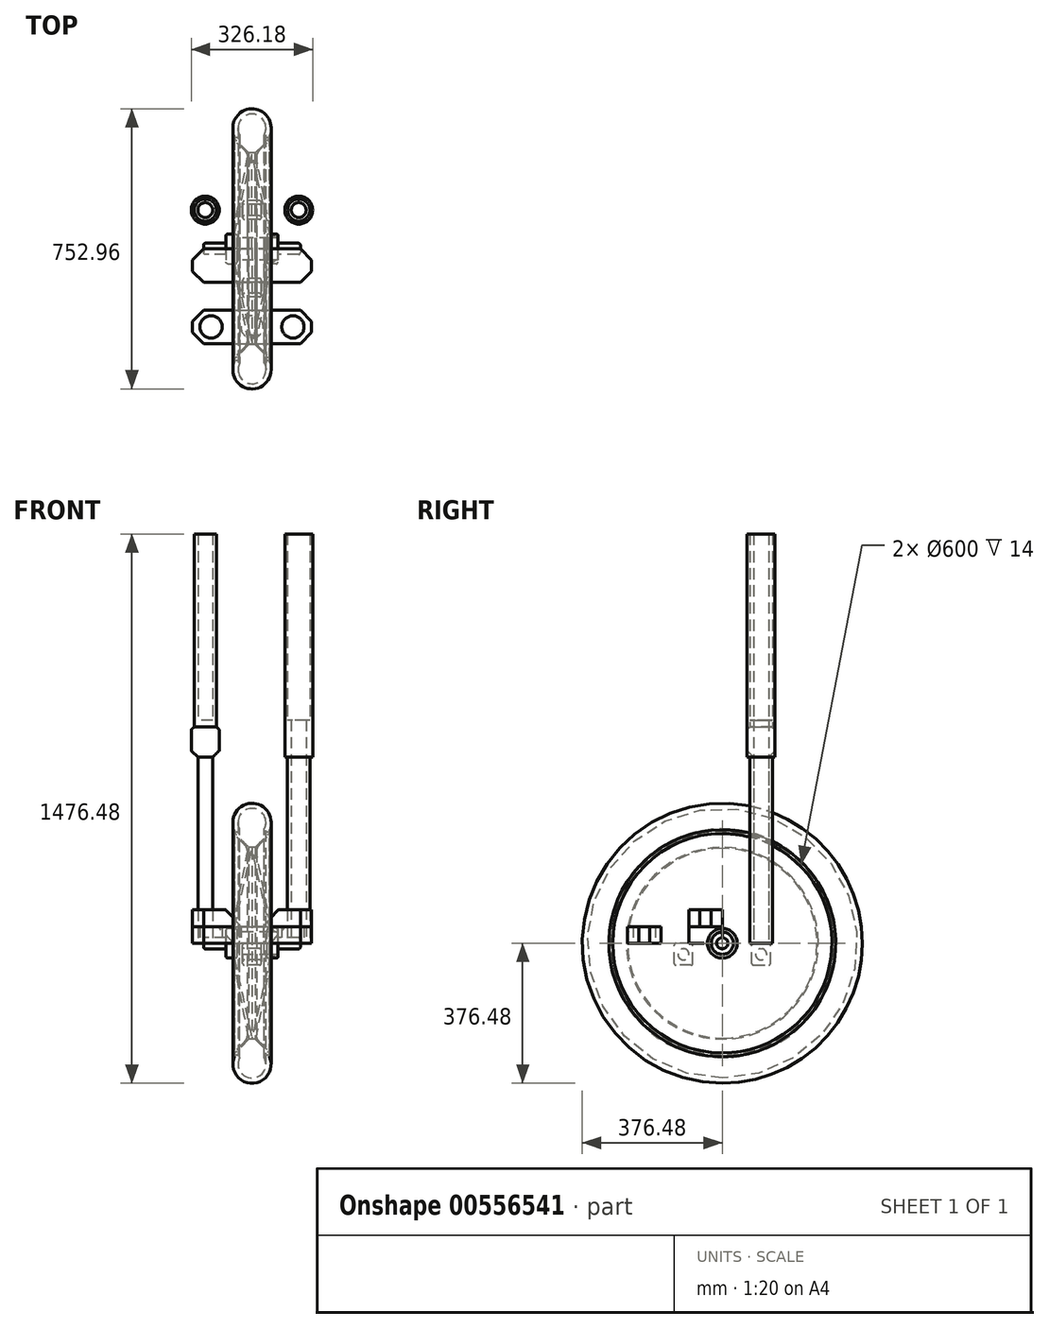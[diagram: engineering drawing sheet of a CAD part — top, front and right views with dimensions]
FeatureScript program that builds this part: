
annotation { "Feature Type Name" : "Feature", "Feature Type Description" : "" }
export const myFeature = defineFeature(function(context is Context, id is Id, definition is map)
    precondition{}
    {
        {
            var Q0;
            Q0=qCreatedBy(makeId("Front.planeOp"),FACE);
            var sketch = newSketch(context, id + "F0", { "sketchPlane" : qUnion([Q0])});
            skLineSegment(sketch, "E0", {"start": v(0, 0) * mm, "end": v(0, 304.8) * mm, "construction": true});
            skLineSegment(sketch, "E1", {"start": v(0, 0) * mm, "end": v(0, 254.8) * mm, "construction": true});
            skLineSegment(sketch, "E2", {"start": v(0, 304.8) * mm, "end": v(-50, 304.8) * mm, "construction": true});
            skLineSegment(sketch, "E3", {"start": v(0, 304.8) * mm, "end": v(50, 304.8) * mm, "construction": true});
            skPoint(sketch, "E4", {"position": v(-50, 304.8) * mm});
            skPoint(sketch, "E5", {"position": v(50, 304.8) * mm});
            skLineSegment(sketch, "E6", {"start": v(-50, 294.8) * mm, "end": v(-10, 254.8) * mm});
            skLineSegment(sketch, "E7", {"start": v(-50, 294.8) * mm, "end": v(-50, 304.8) * mm});
            skLineSegment(sketch, "E8", {"start": v(-10, 254.8) * mm, "end": v(0, 254.8) * mm});
            skLineSegment(sketch, "E9", {"start": v(50, 304.8) * mm, "end": v(50, 294.8) * mm});
            skLineSegment(sketch, "E10", {"start": v(50, 294.8) * mm, "end": v(10, 254.8) * mm});
            skLineSegment(sketch, "E11", {"start": v(10, 254.8) * mm, "end": v(0, 254.8) * mm});
            skLineSegment(sketch, "E12.0", {"start": v(-47, 296.04) * mm, "end": v(-47, 304.8) * mm});
            skLineSegment(sketch, "E12.1", {"start": v(-47, 296.04) * mm, "end": v(-8.76, 257.8) * mm});
            skLineSegment(sketch, "E12.2", {"start": v(47, 304.8) * mm, "end": v(47, 296.04) * mm});
            skLineSegment(sketch, "E12.3", {"start": v(47, 296.04) * mm, "end": v(8.76, 257.8) * mm});
            skLineSegment(sketch, "E12.4", {"start": v(8.76, 257.8) * mm, "end": v(0, 257.8) * mm});
            skLineSegment(sketch, "E12.5", {"start": v(-8.76, 257.8) * mm, "end": v(0, 257.8) * mm});
            skLineSegment(sketch, "E13", {"start": v(-47, 304.8) * mm, "end": v(-50, 304.8) * mm});
            skLineSegment(sketch, "E14", {"start": v(47, 304.8) * mm, "end": v(50, 304.8) * mm});
            skLineSegment(sketch, "E15", {"start": v(0, 0) * mm, "end": v(125, 0) * mm, "construction": true});
            skLineSegment(sketch, "E16", {"start": v(-10, 254.8) * mm, "end": v(-55.27, 19.77) * mm});
            skLineSegment(sketch, "E17", {"start": v(-55.27, 19.77) * mm, "end": v(-52.26, 19.55) * mm});
            skLineSegment(sketch, "E18", {"start": v(-52.26, 19.55) * mm, "end": v(0, 254.8) * mm});
            skLineSegment(sketch, "E19.MirrorCS", {"start": v(52.26, 19.55) * mm, "end": v(0, 254.8) * mm});
            skLineSegment(sketch, "E20.MirrorCS", {"start": v(10, 254.8) * mm, "end": v(55.27, 19.77) * mm});
            skLineSegment(sketch, "E21.MirrorCS", {"start": v(55.27, 19.77) * mm, "end": v(52.26, 19.55) * mm});
            skSolve(sketch);
        }
        {
            var Q0;
            Q0=qSketchRegion(id+"F0",true);
            var Q1;
            Q1=sQuery(id+"F0.wireOp",EDGE,"E15");
            revolve(context, id + "F1", {"entities" : qUnion([Q0]), "axis" : qUnion([Q1]), "revolveType" : RevolveType.FULL});
        }
        {
            var Q0;
            Q0=qCreatedBy(makeId("Right.planeOp"),FACE);
            var sketch = newSketch(context, id + "F2", { "sketchPlane" : qUnion([Q0])});
            skCircle(sketch, "E22", {"center": v(0, 0) * mm, "radius": 15 * mm});
            skSolve(sketch);
        }
        {
            var Q0;
            Q0=qSketchRegion(id+"F2",true);
            extrude(context, id + "F3", {"entities" : qUnion([Q0]), "endBound" : BoundingType.SYMMETRIC, "depth" : 260 * mm, "offsetDistance" : 25 * mm});
        }
        {
            var Q0;
            Q0=qCreatedBy(makeId("Right.planeOp"),FACE);
            var sketch = newSketch(context, id + "F4", { "sketchPlane" : qUnion([Q0])});
            skCircle(sketch, "E23", {"center": v(0, 0) * mm, "radius": 15 * mm});
            skCircle(sketch, "E24", {"center": v(0, 0) * mm, "radius": 20 * mm});
            skCircle(sketch, "E25", {"center": v(0, 0) * mm, "radius": 30 * mm});
            skCircle(sketch, "E26", {"center": v(0, 0) * mm, "radius": 40 * mm});
            skPoint(sketch, "E27", {"position": v(0, 32.5) * mm});
            skLineSegment(sketch, "E28", {"start": v(0, 0) * mm, "end": v(11.12, 30.54) * mm, "construction": true});
            skPoint(sketch, "E29", {"position": v(11.12, 30.54) * mm});
            skLineSegment(sketch, "E30", {"start": v(0, 0) * mm, "end": v(20.9, 24.9) * mm, "construction": true});
            skLineSegment(sketch, "E31", {"start": v(0, 0) * mm, "end": v(28.15, 16.25) * mm, "construction": true});
            skLineSegment(sketch, "E32", {"start": v(0, 0) * mm, "end": v(32, 5.64) * mm, "construction": true});
            skLineSegment(sketch, "E33", {"start": v(0, 0) * mm, "end": v(32, -5.64) * mm, "construction": true});
            skLineSegment(sketch, "E34", {"start": v(0, 0) * mm, "end": v(28.15, -16.25) * mm, "construction": true});
            skLineSegment(sketch, "E35", {"start": v(0, 0) * mm, "end": v(20.9, -24.9) * mm, "construction": true});
            skLineSegment(sketch, "E36", {"start": v(0, 0) * mm, "end": v(0, -32.5) * mm, "construction": true});
            skLineSegment(sketch, "E37", {"start": v(0, 0) * mm, "end": v(-11.12, -30.54) * mm, "construction": true});
            skLineSegment(sketch, "E38", {"start": v(0, 0) * mm, "end": v(-20.9, -24.9) * mm, "construction": true});
            skLineSegment(sketch, "E39", {"start": v(0, 0) * mm, "end": v(-32, -5.64) * mm, "construction": true});
            skLineSegment(sketch, "E40", {"start": v(0, 0) * mm, "end": v(-32, 5.64) * mm, "construction": true});
            skLineSegment(sketch, "E41", {"start": v(0, 0) * mm, "end": v(-20.9, 24.9) * mm, "construction": true});
            skLineSegment(sketch, "E42", {"start": v(0, 0) * mm, "end": v(-28.15, -16.25) * mm, "construction": true});
            skLineSegment(sketch, "E43", {"start": v(0, 0) * mm, "end": v(11.12, -30.54) * mm, "construction": true});
            skLineSegment(sketch, "E44", {"start": v(0, 0) * mm, "end": v(-28.15, 16.25) * mm, "construction": true});
            skLineSegment(sketch, "E45", {"start": v(0, 0) * mm, "end": v(-11.12, 30.54) * mm, "construction": true});
            skPoint(sketch, "E46", {"position": v(20.9, 24.9) * mm});
            skPoint(sketch, "E47", {"position": v(28.15, 16.25) * mm});
            skPoint(sketch, "E48", {"position": v(32, 5.64) * mm});
            skPoint(sketch, "E49", {"position": v(32, -5.64) * mm});
            skPoint(sketch, "E50", {"position": v(28.15, -16.25) * mm});
            skPoint(sketch, "E51", {"position": v(20.9, -24.9) * mm});
            skPoint(sketch, "E52", {"position": v(11.12, -30.54) * mm});
            skPoint(sketch, "E53", {"position": v(0, -32.5) * mm});
            skPoint(sketch, "E54", {"position": v(-11.12, -30.54) * mm});
            skPoint(sketch, "E55", {"position": v(-20.9, -24.9) * mm});
            skPoint(sketch, "E56", {"position": v(-28.15, -16.25) * mm});
            skPoint(sketch, "E57", {"position": v(-32, -5.64) * mm});
            skPoint(sketch, "E58", {"position": v(-32, 5.64) * mm});
            skPoint(sketch, "E59", {"position": v(-28.15, 16.25) * mm});
            skPoint(sketch, "E60", {"position": v(-20.9, 24.9) * mm});
            skPoint(sketch, "E61", {"position": v(-11.12, 30.54) * mm});
            skSolve(sketch);
        }
        {
            var Q0;
            Q0=makeQuery(id+"F4.imprint","IMPRINT",FACE,{"disambiguationData":[TD([[makeQuery(id+"F4.imprint","IMPRINT",EDGE,{"derivedFrom":sQuery(id+"F4.wireOp",EDGE,"E23")}),-1.0]])]});
            extrude(context, id + "F5", {"entities" : qUnion([Q0]), "operationType" : NewBodyOperationType.ADD, "endBound" : BoundingType.SYMMETRIC, "depth" : 140 * mm, "offsetDistance" : 25 * mm});
        }
        {
            var Q0;
            Q0=makeQuery(id+"F4.imprint","IMPRINT",FACE,{"disambiguationData":[TD([[makeQuery(id+"F4.imprint","IMPRINT",EDGE,{"derivedFrom":sQuery(id+"F4.wireOp",EDGE,"E24")}),-1.0]])]});
            extrude(context, id + "F6", {"entities" : qUnion([Q0]), "operationType" : NewBodyOperationType.ADD, "endBound" : BoundingType.SYMMETRIC, "depth" : 140 * mm, "offsetDistance" : 25 * mm});
        }
        {
            var Q0;
            Q0=makeQuery(id+"F4.imprint","IMPRINT",FACE,{"disambiguationData":[TD([[makeQuery(id+"F4.imprint","IMPRINT",EDGE,{"derivedFrom":sQuery(id+"F4.wireOp",EDGE,"E25")}),-1.0]])]});
            var Q1;
            Q1=makeQuery(id+"F5.opExtrude","CAP_FACE",FACE,{"disambiguationData":[OSD([sQuery(id+"F4.wireOp",EDGE,"E23"),sQuery(id+"F4.wireOp",EDGE,"E24")])],"isStart":false});
            extrude(context, id + "F7", {"entities" : qUnion([Q0]), "endBound" : BoundingType.UP_TO_SURFACE, "depth" : 182 * mm, "endBoundEntityFace" : qUnion([Q1]), "offsetDistance" : 25 * mm, "hasSecondDirection" : true, "secondDirectionOppositeDirection" : false, "secondDirectionDepth" : 40 * mm});
        }
        {
            var Q0;
            Q0=makeQuery(id+"F4.imprint","IMPRINT",FACE,{"disambiguationData":[TD([[makeQuery(id+"F4.imprint","IMPRINT",EDGE,{"derivedFrom":sQuery(id+"F4.wireOp",EDGE,"E25")}),-1.0]])]});
            var Q1;
            Q1=makeQuery(id+"F5.opExtrude","CAP_FACE",FACE,{"disambiguationData":[OSD([sQuery(id+"F4.wireOp",EDGE,"E23"),sQuery(id+"F4.wireOp",EDGE,"E24")])],"isStart":true});
            extrude(context, id + "F8", {"entities" : qUnion([Q0]), "operationType" : NewBodyOperationType.ADD, "endBound" : BoundingType.UP_TO_SURFACE, "oppositeDirection" : true, "depth" : 25 * mm, "endBoundEntityFace" : qUnion([Q1]), "offsetDistance" : 25 * mm, "hasSecondDirection" : true, "secondDirectionOppositeDirection" : true, "secondDirectionDepth" : 40 * mm});
        }
        {
            var Q0;
            Q0=makeQuery(id+"F3.opExtrude","CAP_EDGE",EDGE,{"disambiguationData":[OSD([sQuery(id+"F2.wireOp",EDGE,"E22")])],"isStart":false});
            var Q1;
            Q1=makeQuery(id+"F3.opExtrude","CAP_EDGE",EDGE,{"disambiguationData":[OSD([sQuery(id+"F2.wireOp",EDGE,"E22")])],"isStart":true});
            var Q2;
            Q2=makeQuery(id+"F6.opExtrude","CAP_EDGE",EDGE,{"disambiguationData":[OSD([sQuery(id+"F4.wireOp",EDGE,"E25")])],"isStart":true});
            var Q3;
            Q3=makeQuery(id+"F6.opExtrude","CAP_EDGE",EDGE,{"disambiguationData":[OSD([sQuery(id+"F4.wireOp",EDGE,"E25")])],"isStart":false});
            var Q4;
            Q4=makeQuery(id+"F8.opExtrude","CAP_EDGE",EDGE,{"disambiguationData":[OSD([sQuery(id+"F4.wireOp",EDGE,"E26")])],"isStart":false});
            var Q5;
            Q5=makeQuery(id+"F8.opExtrude","CAP_EDGE",EDGE,{"disambiguationData":[OSD([sQuery(id+"F4.wireOp",EDGE,"E26")])],"isStart":true});
            var Q6;
            Q6=makeQuery(id+"F7.opExtrude","CAP_EDGE",EDGE,{"disambiguationData":[OSD([sQuery(id+"F4.wireOp",EDGE,"E26")])],"isStart":true});
            var Q7;
            Q7=makeQuery(id+"F7.opExtrude","CAP_EDGE",EDGE,{"disambiguationData":[OSD([sQuery(id+"F4.wireOp",EDGE,"E26")])],"isStart":false});
            fillet(context, id + "F9", {"entities" : qUnion([Q0, Q1, Q2, Q3, Q4, Q5, Q6, Q7]), "radius" : 5 * mm, "tangentPropagation" : true, "allowEdgeOverflow" : false});
        }
        {
            var Q0;
            Q0=qCreatedBy(makeId("Top.planeOp"),FACE);
            var sketch = newSketch(context, id + "F10", { "sketchPlane" : qUnion([Q0])});
            skCircle(sketch, "E62", {"center": v(-125.6, 104.3) * mm, "radius": 20 * mm});
            skCircle(sketch, "E63", {"center": v(-125.6, 104.3) * mm, "radius": 30 * mm});
            skCircle(sketch, "E64", {"center": v(-125.6, 104.3) * mm, "radius": 37.5 * mm});
            skCircle(sketch, "E65.MirrorC", {"center": v(125.6, 104.3) * mm, "radius": 30 * mm});
            skCircle(sketch, "E66.MirrorC", {"center": v(125.6, 104.3) * mm, "radius": 20 * mm});
            skCircle(sketch, "E67.MirrorC", {"center": v(125.6, 104.3) * mm, "radius": 37.5 * mm});
            skSolve(sketch);
        }
        {
            var Q0;
            Q0=makeQuery(id+"F10.imprint","IMPRINT",FACE,{"disambiguationData":[TD([[makeQuery(id+"F10.imprint","IMPRINT",EDGE,{"derivedFrom":sQuery(id+"F10.wireOp",EDGE,"E62")}),1.0]])]});
            var Q1;
            Q1=makeQuery(id+"F10.imprint","IMPRINT",FACE,{"disambiguationData":[TD([[makeQuery(id+"F10.imprint","IMPRINT",EDGE,{"derivedFrom":sQuery(id+"F10.wireOp",EDGE,"E66.MirrorC")}),-1.0]])]});
            extrude(context, id + "F11", {"entities" : qUnion([Q0, Q1]), "depth" : 600 * mm, "offsetDistance" : 25 * mm});
        }
        {
            var Q0;
            Q0=makeQuery(id+"F10.imprint","IMPRINT",FACE,{"disambiguationData":[TD([[makeQuery(id+"F10.imprint","IMPRINT",EDGE,{"derivedFrom":sQuery(id+"F10.wireOp",EDGE,"E62")}),-1.0]])]});
            var Q1;
            Q1=makeQuery(id+"F10.imprint","IMPRINT",FACE,{"disambiguationData":[TD([[makeQuery(id+"F10.imprint","IMPRINT",EDGE,{"derivedFrom":sQuery(id+"F10.wireOp",EDGE,"E65.MirrorC")}),-1.0]])]});
            extrude(context, id + "F12", {"entities" : qUnion([Q0, Q1]), "operationType" : NewBodyOperationType.ADD, "depth" : 1100 * mm, "offsetDistance" : 25 * mm, "hasSecondDirection" : true, "secondDirectionOppositeDirection" : false, "secondDirectionDepth" : 500 * mm});
        }
        {
            var Q0;
            Q0=qCreatedBy(makeId("Right.planeOp"),FACE);
            var sketch = newSketch(context, id + "F13", { "sketchPlane" : qUnion([Q0])});
            skLineSegment(sketch, "E68.bottom", {"start": v(79.37, -59.12) * mm, "end": v(129.37, -59.12) * mm});
            skLineSegment(sketch, "E68.top", {"start": v(79.37, -0.19) * mm, "end": v(129.37, -0.19) * mm});
            skLineSegment(sketch, "E68.left", {"start": v(79.37, -59.12) * mm, "end": v(79.37, -0.19) * mm});
            skLineSegment(sketch, "E68.right", {"start": v(129.37, -59.12) * mm, "end": v(129.37, -0.19) * mm});
            skPoint(sketch, "E68.middle", {"position": v(104.37, -29.65) * mm});
            skCircle(sketch, "E69", {"center": v(104.37, -29.65) * mm, "radius": 15 * mm});
            skPoint(sketch, "E70.MirrorP", {"position": v(-104.37, -29.65) * mm});
            skLineSegment(sketch, "E71.MirrorCS", {"start": v(-129.37, -59.12) * mm, "end": v(-129.37, -0.19) * mm});
            skCircle(sketch, "E72.MirrorC", {"center": v(-104.37, -29.65) * mm, "radius": 15 * mm});
            skLineSegment(sketch, "E73.MirrorCS", {"start": v(-79.37, -59.12) * mm, "end": v(-129.37, -59.12) * mm});
            skLineSegment(sketch, "E74.MirrorCS", {"start": v(-79.37, -59.12) * mm, "end": v(-79.37, -0.19) * mm});
            skLineSegment(sketch, "E75.MirrorCS", {"start": v(-79.37, -0.19) * mm, "end": v(-129.37, -0.19) * mm});
            skSolve(sketch);
        }
        {
            var Q0;
            Q0 = qSketchRegion(id + "F13", true);
            extrude(context, id + "F14", {"entities" : qUnion([Q0]), "endBound" : BoundingType.SYMMETRIC, "depth" : 50 * mm, "offsetDistance" : 25 * mm});
        }
        {
            var Q0;
            Q0=makeQuery(id+"F14.opExtrude","CAP_EDGE",EDGE,{"disambiguationData":[OSD([sQuery(id+"F13.wireOp",EDGE,"E68.top")])],"isStart":false});
            var Q1;
            Q1=makeQuery(id+"F14.opExtrude","SWEPT_EDGE",EDGE,{"disambiguationData":[OSD([sQuery(id+"F13.wireOp",EDGE,"E68.top"),sQuery(id+"F13.wireOp",EDGE,"E68.left")])]});
            var Q2;
            Q2=makeQuery(id+"F14.opExtrude","CAP_EDGE",EDGE,{"disambiguationData":[OSD([sQuery(id+"F13.wireOp",EDGE,"E68.top")])],"isStart":true});
            var Q3;
            Q3=makeQuery(id+"F14.opExtrude","SWEPT_EDGE",EDGE,{"disambiguationData":[OSD([sQuery(id+"F13.wireOp",EDGE,"E68.top"),sQuery(id+"F13.wireOp",EDGE,"E68.right")])]});
            var Q4;
            Q4=makeQuery(id+"F14.opExtrude","SWEPT_FACE",FACE,{"disambiguationData":[OSD([sQuery(id+"F13.wireOp",EDGE,"E68.left")])]});
            var Q5;
            Q5=makeQuery(id+"F14.opExtrude","CAP_FACE",FACE,{"disambiguationData":[OSD([sQuery(id+"F13.wireOp",EDGE,"E68.bottom"),sQuery(id+"F13.wireOp",EDGE,"E68.top"),sQuery(id+"F13.wireOp",EDGE,"E68.left"),sQuery(id+"F13.wireOp",EDGE,"E68.right"),sQuery(id+"F13.wireOp",EDGE,"E69")])],"isStart":false});
            var Q6;
            Q6=makeQuery(id+"F14.opExtrude","SWEPT_FACE",FACE,{"disambiguationData":[OSD([sQuery(id+"F13.wireOp",EDGE,"E68.right")])]});
            var Q7;
            Q7=makeQuery(id+"F14.opExtrude","CAP_FACE",FACE,{"disambiguationData":[OSD([sQuery(id+"F13.wireOp",EDGE,"E68.bottom"),sQuery(id+"F13.wireOp",EDGE,"E68.top"),sQuery(id+"F13.wireOp",EDGE,"E68.left"),sQuery(id+"F13.wireOp",EDGE,"E68.right"),sQuery(id+"F13.wireOp",EDGE,"E69")])],"isStart":true});
            var Q8;
            Q8=makeQuery(id+"F14.opExtrude","CAP_EDGE",EDGE,{"disambiguationData":[OSD([sQuery(id+"F13.wireOp",EDGE,"E72.MirrorC")])],"isStart":false});
            var Q9;
            Q9=makeQuery(id+"F14.opExtrude","CAP_EDGE",EDGE,{"disambiguationData":[OSD([sQuery(id+"F13.wireOp",EDGE,"E71.MirrorCS")])],"isStart":false});
            var Q10;
            Q10=makeQuery(id+"F14.opExtrude","CAP_EDGE",EDGE,{"disambiguationData":[OSD([sQuery(id+"F13.wireOp",EDGE,"E74.MirrorCS")])],"isStart":false});
            var Q11;
            Q11=makeQuery(id+"F14.opExtrude","CAP_EDGE",EDGE,{"disambiguationData":[OSD([sQuery(id+"F13.wireOp",EDGE,"E72.MirrorC")])],"isStart":true});
            var Q12;
            Q12=makeQuery(id+"F14.opExtrude","CAP_EDGE",EDGE,{"disambiguationData":[OSD([sQuery(id+"F13.wireOp",EDGE,"E75.MirrorCS")])],"isStart":false});
            var Q13;
            Q13=makeQuery(id+"F14.opExtrude","CAP_EDGE",EDGE,{"disambiguationData":[OSD([sQuery(id+"F13.wireOp",EDGE,"E73.MirrorCS")])],"isStart":false});
            var Q14;
            Q14=makeQuery(id+"F14.opExtrude","CAP_EDGE",EDGE,{"disambiguationData":[OSD([sQuery(id+"F13.wireOp",EDGE,"E74.MirrorCS")])],"isStart":true});
            var Q15;
            Q15=makeQuery(id+"F14.opExtrude","SWEPT_EDGE",EDGE,{"disambiguationData":[OSD([sQuery(id+"F13.wireOp",EDGE,"E73.MirrorCS"),sQuery(id+"F13.wireOp",EDGE,"E74.MirrorCS")])]});
            var Q16;
            Q16=makeQuery(id+"F14.opExtrude","SWEPT_EDGE",EDGE,{"disambiguationData":[OSD([sQuery(id+"F13.wireOp",EDGE,"E71.MirrorCS"),sQuery(id+"F13.wireOp",EDGE,"E73.MirrorCS")])]});
            var Q17;
            Q17=makeQuery(id+"F14.opExtrude","SWEPT_EDGE",EDGE,{"disambiguationData":[OSD([sQuery(id+"F13.wireOp",EDGE,"E71.MirrorCS"),sQuery(id+"F13.wireOp",EDGE,"E75.MirrorCS")])]});
            var Q18;
            Q18=makeQuery(id+"F14.opExtrude","CAP_EDGE",EDGE,{"disambiguationData":[OSD([sQuery(id+"F13.wireOp",EDGE,"E71.MirrorCS")])],"isStart":true});
            var Q19;
            Q19=makeQuery(id+"F14.opExtrude","SWEPT_EDGE",EDGE,{"disambiguationData":[OSD([sQuery(id+"F13.wireOp",EDGE,"E74.MirrorCS"),sQuery(id+"F13.wireOp",EDGE,"E75.MirrorCS")])]});
            var Q20;
            Q20=makeQuery(id+"F14.opExtrude","CAP_EDGE",EDGE,{"disambiguationData":[OSD([sQuery(id+"F13.wireOp",EDGE,"E75.MirrorCS")])],"isStart":true});
            var Q21;
            Q21=makeQuery(id+"F14.opExtrude","CAP_EDGE",EDGE,{"disambiguationData":[OSD([sQuery(id+"F13.wireOp",EDGE,"E73.MirrorCS")])],"isStart":true});
            fillet(context, id + "F15", {"entities" : qUnion([Q0, Q1, Q2, Q3, Q4, Q5, Q6, Q7, Q8, Q9, Q10, Q11, Q12, Q13, Q14, Q15, Q16, Q17, Q18, Q19, Q20, Q21]), "radius" : 5 * mm, "tangentPropagation" : true, "allowEdgeOverflow" : false});
        }
        {
            var Q0;
            Q0=makeQuery(id+"F1.opRevolve","SWEPT_FACE",FACE,{"disambiguationData":[OSD([sQuery(id+"F0.wireOp",EDGE,"E20.MirrorCS")])]});
            var Q1;
            Q1=makeQuery(id+"F1.opRevolve","SWEPT_EDGE",EDGE,{"disambiguationData":[OSD([sQuery(id+"F0.wireOp",EDGE,"E6"),sQuery(id+"F0.wireOp",EDGE,"E8"),sQuery(id+"F0.wireOp",EDGE,"E16")])]});
            fillet(context, id + "F16", {"entities" : qUnion([Q0, Q1]), "radius" : 25 * mm, "tangentPropagation" : true, "allowEdgeOverflow" : false});
        }
        {
            var Q0;
            Q0=makeQuery(id+"F12.opExtrude","CAP_EDGE",EDGE,{"disambiguationData":[OSD([sQuery(id+"F10.wireOp",EDGE,"E63")])],"isStart":true});
            var Q1;
            Q1=makeQuery(id+"F12.opExtrude","CAP_EDGE",EDGE,{"disambiguationData":[OSD([sQuery(id+"F10.wireOp",EDGE,"E65.MirrorC")])],"isStart":true});
            chamfer(context, id + "F17", {"entities" : qUnion([Q0, Q1]), "width" : 10 * mm, "tangentPropagation" : true});
        }
        {
            var Q0;
            Q0=makeQuery(id+"F10.imprint","IMPRINT",FACE,{"disambiguationData":[TD([[makeQuery(id+"F10.imprint","IMPRINT",EDGE,{"derivedFrom":sQuery(id+"F10.wireOp",EDGE,"E63")}),-1.0]])]});
            var Q1;
            Q1=makeQuery(id+"F10.imprint","IMPRINT",FACE,{"disambiguationData":[TD([[makeQuery(id+"F10.imprint","IMPRINT",EDGE,{"derivedFrom":sQuery(id+"F10.wireOp",EDGE,"E65.MirrorC")}),1.0]])]});
            extrude(context, id + "F18", {"entities" : qUnion([Q0, Q1]), "operationType" : NewBodyOperationType.ADD, "depth" : 581 * mm, "offsetDistance" : 25 * mm, "hasSecondDirection" : true, "secondDirectionOppositeDirection" : false, "secondDirectionDepth" : 509 * mm});
        }
        {
            var Q0;
            Q0=makeQuery(id+"F18.opExtrude","CAP_EDGE",EDGE,{"disambiguationData":[OSD([sQuery(id+"F10.wireOp",EDGE,"E64")])],"isStart":true});
            var Q1;
            Q1=makeQuery(id+"F18.opExtrude","CAP_EDGE",EDGE,{"disambiguationData":[OSD([sQuery(id+"F10.wireOp",EDGE,"E67.MirrorC")])],"isStart":true});
            chamfer(context, id + "F19", {"entities" : qUnion([Q0, Q1]), "width" : 8.5 * mm, "tangentPropagation" : true});
        }
        {
            var Q0;
            Q0=makeQuery(id+"F18.opExtrude","CAP_EDGE",EDGE,{"disambiguationData":[OSD([sQuery(id+"F10.wireOp",EDGE,"E64")])],"isStart":false});
            var Q1;
            Q1=makeQuery(id+"F18.opExtrude","CAP_EDGE",EDGE,{"disambiguationData":[OSD([sQuery(id+"F10.wireOp",EDGE,"E67.MirrorC")])],"isStart":false});
            chamfer(context, id + "F20", {"entities" : qUnion([Q0, Q1]), "width" : 7 * mm, "tangentPropagation" : true});
        }
        {
            var Q0;
            {var subQ0=sQuery(id+"F10.wireOp",EDGE,"E64");Q0=makeQuery(id+"F20.opChamfer","BLEND_EDGE",EDGE,{"blendedFrom":[makeQuery(id+"F18.opExtrude","CAP_EDGE",EDGE,{"disambiguationData":[OSD([subQ0])],"isStart":false}),makeQuery(id+"F18.opExtrude","CAP_FACE",FACE,{"disambiguationData":[OSD([sQuery(id+"F10.wireOp",EDGE,"E63"),subQ0])],"isStart":false})],"blendedInto":[makeQuery(id+"F18.opExtrude","CAP_FACE",FACE,{"disambiguationData":[OSD([sQuery(id+"F10.wireOp",EDGE,"E63"),subQ0])],"isStart":false})]});}
            var Q1;
            {var subQ0=sQuery(id+"F10.wireOp",EDGE,"E64");Q1=makeQuery(id+"F20.opChamfer","BLEND_EDGE",EDGE,{"blendedFrom":[makeQuery(id+"F18.opExtrude","CAP_EDGE",EDGE,{"disambiguationData":[OSD([subQ0])],"isStart":false}),makeQuery(id+"F18.opExtrude","SWEPT_FACE",FACE,{"disambiguationData":[OSD([subQ0])]})],"blendedInto":[makeQuery(id+"F18.opExtrude","SWEPT_FACE",FACE,{"disambiguationData":[OSD([subQ0])]})]});}
            var Q2;
            {var subQ0=sQuery(id+"F10.wireOp",EDGE,"E64");Q2=makeQuery(id+"F19.opChamfer","BLEND_EDGE",EDGE,{"blendedFrom":[makeQuery(id+"F18.opExtrude","CAP_EDGE",EDGE,{"disambiguationData":[OSD([subQ0])],"isStart":true}),makeQuery(id+"F18.opExtrude","SWEPT_FACE",FACE,{"disambiguationData":[OSD([subQ0])]})],"blendedInto":[makeQuery(id+"F18.opExtrude","SWEPT_FACE",FACE,{"disambiguationData":[OSD([subQ0])]})]});}
            var Q3;
            {var subQ0=sQuery(id+"F10.wireOp",EDGE,"E67.MirrorC");Q3=makeQuery(id+"F19.opChamfer","BLEND_EDGE",EDGE,{"blendedFrom":[makeQuery(id+"F18.opExtrude","CAP_EDGE",EDGE,{"disambiguationData":[OSD([subQ0])],"isStart":true}),makeQuery(id+"F18.opExtrude","SWEPT_FACE",FACE,{"disambiguationData":[OSD([subQ0])]})],"blendedInto":[makeQuery(id+"F18.opExtrude","SWEPT_FACE",FACE,{"disambiguationData":[OSD([subQ0])]})]});}
            var Q4;
            {var subQ0=sQuery(id+"F10.wireOp",EDGE,"E67.MirrorC");Q4=makeQuery(id+"F20.opChamfer","BLEND_EDGE",EDGE,{"blendedFrom":[makeQuery(id+"F18.opExtrude","CAP_EDGE",EDGE,{"disambiguationData":[OSD([subQ0])],"isStart":false}),makeQuery(id+"F18.opExtrude","CAP_FACE",FACE,{"disambiguationData":[OSD([sQuery(id+"F10.wireOp",EDGE,"E65.MirrorC"),subQ0])],"isStart":false})],"blendedInto":[makeQuery(id+"F18.opExtrude","CAP_FACE",FACE,{"disambiguationData":[OSD([sQuery(id+"F10.wireOp",EDGE,"E65.MirrorC"),subQ0])],"isStart":false})]});}
            var Q5;
            {var subQ0=sQuery(id+"F10.wireOp",EDGE,"E67.MirrorC");Q5=makeQuery(id+"F20.opChamfer","BLEND_EDGE",EDGE,{"blendedFrom":[makeQuery(id+"F18.opExtrude","CAP_EDGE",EDGE,{"disambiguationData":[OSD([subQ0])],"isStart":false}),makeQuery(id+"F18.opExtrude","SWEPT_FACE",FACE,{"disambiguationData":[OSD([subQ0])]})],"blendedInto":[makeQuery(id+"F18.opExtrude","SWEPT_FACE",FACE,{"disambiguationData":[OSD([subQ0])]})]});}
            fillet(context, id + "F21", {"entities" : qUnion([Q0, Q1, Q2, Q3, Q4, Q5]), "radius" : 3 * mm, "tangentPropagation" : true, "allowEdgeOverflow" : false});
        }
        {
            var Q0;
            Q0=qCreatedBy(makeId("Top.planeOp"),FACE);
            var sketch = newSketch(context, id + "F22", { "sketchPlane" : qUnion([Q0])});
            skLineSegment(sketch, "E76.bottom", {"start": v(-160, -164.8) * mm, "end": v(160, -164.8) * mm});
            skLineSegment(sketch, "E76.top", {"start": v(-160, -254.8) * mm, "end": v(160, -254.8) * mm});
            skLineSegment(sketch, "E76.left", {"start": v(-160, -164.8) * mm, "end": v(-160, -254.8) * mm});
            skLineSegment(sketch, "E76.right", {"start": v(160, -164.8) * mm, "end": v(160, -254.8) * mm});
            skPoint(sketch, "E76.middle", {"position": v(0, -209.8) * mm});
            skCircle(sketch, "E77", {"center": v(0, -209.8) * mm, "radius": 30 * mm});
            skLineSegment(sketch, "E78", {"start": v(0, -209.8) * mm, "end": v(-110, -209.8) * mm, "construction": true});
            skLineSegment(sketch, "E79", {"start": v(-110, -209.8) * mm, "end": v(0, -209.8) * mm, "construction": true});
            skLineSegment(sketch, "E80", {"start": v(0, -209.8) * mm, "end": v(110, -209.8) * mm, "construction": true});
            skCircle(sketch, "E81", {"center": v(-110, -209.8) * mm, "radius": 30 * mm});
            skCircle(sketch, "E82", {"center": v(110, -209.8) * mm, "radius": 30 * mm});
            skSolve(sketch);
        }
        {
            var Q0;
            Q0 = qSketchRegion(id + "F22", true);
            extrude(context, id + "F23", {"entities" : qUnion([Q0]), "depth" : 45 * mm, "offsetDistance" : 25 * mm});
        }
        {
            var Q0;
            Q0=makeQuery(id+"F23.opExtrude","SWEPT_EDGE",EDGE,{"disambiguationData":[OSD([sQuery(id+"F22.wireOp",EDGE,"E76.bottom"),sQuery(id+"F22.wireOp",EDGE,"E76.left")])]});
            var Q1;
            Q1=makeQuery(id+"F23.opExtrude","SWEPT_EDGE",EDGE,{"disambiguationData":[OSD([sQuery(id+"F22.wireOp",EDGE,"E76.top"),sQuery(id+"F22.wireOp",EDGE,"E76.left")])]});
            var Q2;
            Q2=makeQuery(id+"F23.opExtrude","SWEPT_EDGE",EDGE,{"disambiguationData":[OSD([sQuery(id+"F22.wireOp",EDGE,"E76.bottom"),sQuery(id+"F22.wireOp",EDGE,"E76.right")])]});
            var Q3;
            Q3=makeQuery(id+"F23.opExtrude","SWEPT_EDGE",EDGE,{"disambiguationData":[OSD([sQuery(id+"F22.wireOp",EDGE,"E76.top"),sQuery(id+"F22.wireOp",EDGE,"E76.right")])]});
            chamfer(context, id + "F24", {"entities" : qUnion([Q0, Q1, Q2, Q3]), "width" : 30 * mm, "tangentPropagation" : true});
        }
        {
            var Q0;
            Q0=qCreatedBy(makeId("Front.planeOp"),FACE);
            var sketch = newSketch(context, id + "F25", { "sketchPlane" : qUnion([Q0])});
            skLineSegment(sketch, "E83", {"start": v(0, 0) * mm, "end": v(-50, 0) * mm});
            skLineSegment(sketch, "E84", {"start": v(-50, 0) * mm, "end": v(-90, 0) * mm, "construction": true});
            skLineSegment(sketch, "E85", {"start": v(-50, 0) * mm, "end": v(-90, 44.72) * mm});
            skLineSegment(sketch, "E86", {"start": v(-90, 44.72) * mm, "end": v(-160, 44.72) * mm});
            skLineSegment(sketch, "E87", {"start": v(0, 0) * mm, "end": v(50, 0) * mm});
            skLineSegment(sketch, "E88", {"start": v(50, 0) * mm, "end": v(90, 0) * mm, "construction": true});
            skLineSegment(sketch, "E89", {"start": v(50, 0) * mm, "end": v(90, 44.72) * mm});
            skLineSegment(sketch, "E90", {"start": v(90, 44.72) * mm, "end": v(160, 44.72) * mm});
            skLineSegment(sketch, "E91.0", {"start": v(-69.88, 89.72) * mm, "end": v(-160, 89.72) * mm});
            skLineSegment(sketch, "E91.1", {"start": v(-29.88, 45) * mm, "end": v(-69.88, 89.72) * mm});
            skLineSegment(sketch, "E91.2", {"start": v(69.88, 89.72) * mm, "end": v(160, 89.72) * mm});
            skLineSegment(sketch, "E91.3", {"start": v(29.88, 45) * mm, "end": v(69.88, 89.72) * mm});
            skLineSegment(sketch, "E91.4", {"start": v(0, 45) * mm, "end": v(29.88, 45) * mm});
            skLineSegment(sketch, "E91.5", {"start": v(0, 45) * mm, "end": v(-29.88, 45) * mm});
            skLineSegment(sketch, "E92", {"start": v(-160, 89.72) * mm, "end": v(-160, 44.72) * mm});
            skLineSegment(sketch, "E93", {"start": v(160, 89.72) * mm, "end": v(160, 44.72) * mm});
            skSolve(sketch);
        }
        {
            var Q0;
            Q0 = qSketchRegion(id + "F25", true);
            extrude(context, id + "F26", {"entities" : qUnion([Q0]), "depth" : 90 * mm, "offsetDistance" : 25 * mm});
        }
        {
            var Q0;
            Q0=makeQuery(id+"F26.opExtrude","CAP_EDGE",EDGE,{"disambiguationData":[OSD([sQuery(id+"F25.wireOp",EDGE,"E92")])],"isStart":false});
            var Q1;
            Q1=makeQuery(id+"F26.opExtrude","CAP_EDGE",EDGE,{"disambiguationData":[OSD([sQuery(id+"F25.wireOp",EDGE,"E93")])],"isStart":false});
            var Q2;
            Q2=makeQuery(id+"F26.opExtrude","CAP_EDGE",EDGE,{"disambiguationData":[OSD([sQuery(id+"F25.wireOp",EDGE,"E92")])],"isStart":true});
            var Q3;
            Q3=makeQuery(id+"F26.opExtrude","CAP_EDGE",EDGE,{"disambiguationData":[OSD([sQuery(id+"F25.wireOp",EDGE,"E93")])],"isStart":true});
            chamfer(context, id + "F27", {"entities" : qUnion([Q0, Q1, Q2, Q3]), "width" : 30 * mm, "tangentPropagation" : true});
        }
        {
            var Q0;
            Q0=makeQuery(id+"F26.opExtrude","SWEPT_EDGE",EDGE,{"disambiguationData":[OSD([sQuery(id+"F25.wireOp",EDGE,"E83"),sQuery(id+"F25.wireOp",EDGE,"E85")])]});
            var Q1;
            Q1=makeQuery(id+"F26.opExtrude","SWEPT_EDGE",EDGE,{"disambiguationData":[OSD([sQuery(id+"F25.wireOp",EDGE,"E85"),sQuery(id+"F25.wireOp",EDGE,"E86")])]});
            var Q2;
            Q2=makeQuery(id+"F26.opExtrude","SWEPT_EDGE",EDGE,{"disambiguationData":[OSD([sQuery(id+"F25.wireOp",EDGE,"E87"),sQuery(id+"F25.wireOp",EDGE,"E89")])]});
            var Q3;
            Q3=makeQuery(id+"F26.opExtrude","SWEPT_EDGE",EDGE,{"disambiguationData":[OSD([sQuery(id+"F25.wireOp",EDGE,"E89"),sQuery(id+"F25.wireOp",EDGE,"E90")])]});
            var Q4;
            Q4=makeQuery(id+"F26.opExtrude","SWEPT_EDGE",EDGE,{"disambiguationData":[OSD([sQuery(id+"F25.wireOp",EDGE,"E91.0"),sQuery(id+"F25.wireOp",EDGE,"E91.1")])]});
            var Q5;
            Q5=makeQuery(id+"F26.opExtrude","SWEPT_EDGE",EDGE,{"disambiguationData":[OSD([sQuery(id+"F25.wireOp",EDGE,"E91.1"),sQuery(id+"F25.wireOp",EDGE,"E91.5")])]});
            var Q6;
            Q6=makeQuery(id+"F26.opExtrude","SWEPT_EDGE",EDGE,{"disambiguationData":[OSD([sQuery(id+"F25.wireOp",EDGE,"E91.3"),sQuery(id+"F25.wireOp",EDGE,"E91.4")])]});
            var Q7;
            Q7=makeQuery(id+"F26.opExtrude","SWEPT_EDGE",EDGE,{"disambiguationData":[OSD([sQuery(id+"F25.wireOp",EDGE,"E91.2"),sQuery(id+"F25.wireOp",EDGE,"E91.3")])]});
            fillet(context, id + "F28", {"entities" : qUnion([Q0, Q1, Q2, Q3, Q4, Q5, Q6, Q7]), "radius" : 5 * mm, "tangentPropagation" : true, "allowEdgeOverflow" : false});
        }
        {
            var Q0;
            Q0=qCreatedBy(makeId("Front.planeOp"),FACE);
            var sketch = newSketch(context, id + "F29", { "sketchPlane" : qUnion([Q0])});
            skLineSegment(sketch, "E94", {"start": v(0, 0) * mm, "end": v(0, 300) * mm, "construction": true});
            skLineSegment(sketch, "E95", {"start": v(0, 300) * mm, "end": v(47, 300) * mm, "construction": true});
            skLineSegment(sketch, "E96", {"start": v(0, 300) * mm, "end": v(-47, 300) * mm, "construction": true});
            skLineSegment(sketch, "E97", {"start": v(-47, 300) * mm, "end": v(-47, 304) * mm});
            skLineSegment(sketch, "E98", {"start": v(47, 300) * mm, "end": v(47, 304) * mm});
            skLineSegment(sketch, "E99", {"start": v(0, 300) * mm, "end": v(0, 325) * mm, "construction": true});
            skArc(sketch, "E100", {"start": v(47, 304) * mm, "mid": v(0, 376.48) * mm, "end": v(-47, 304) * mm});
            skLineSegment(sketch, "E101.0", {"start": v(-33, 300) * mm, "end": v(-33, 307.23) * mm});
            skArc(sketch, "E101.1", {"start": v(33, 307.23) * mm, "mid": v(0, 362.48) * mm, "end": v(-33, 307.23) * mm});
            skLineSegment(sketch, "E101.2", {"start": v(33, 300) * mm, "end": v(33, 307.23) * mm});
            skLineSegment(sketch, "E102", {"start": v(-47, 300) * mm, "end": v(-33, 300) * mm});
            skLineSegment(sketch, "E103", {"start": v(47, 300) * mm, "end": v(33, 300) * mm});
            skLineSegment(sketch, "E104", {"start": v(0, 0) * mm, "end": v(-255.58, 0) * mm, "construction": true});
            skSolve(sketch);
        }
        {
            var Q0;
            Q0 = qSketchRegion(id + "F29", true);
            var Q1;
            Q1=sQuery(id+"F29.wireOp",EDGE,"E104");
            revolve(context, id + "F30", {"entities" : qUnion([Q0]), "axis" : qUnion([Q1]), "revolveType" : RevolveType.FULL});
        }
    });
